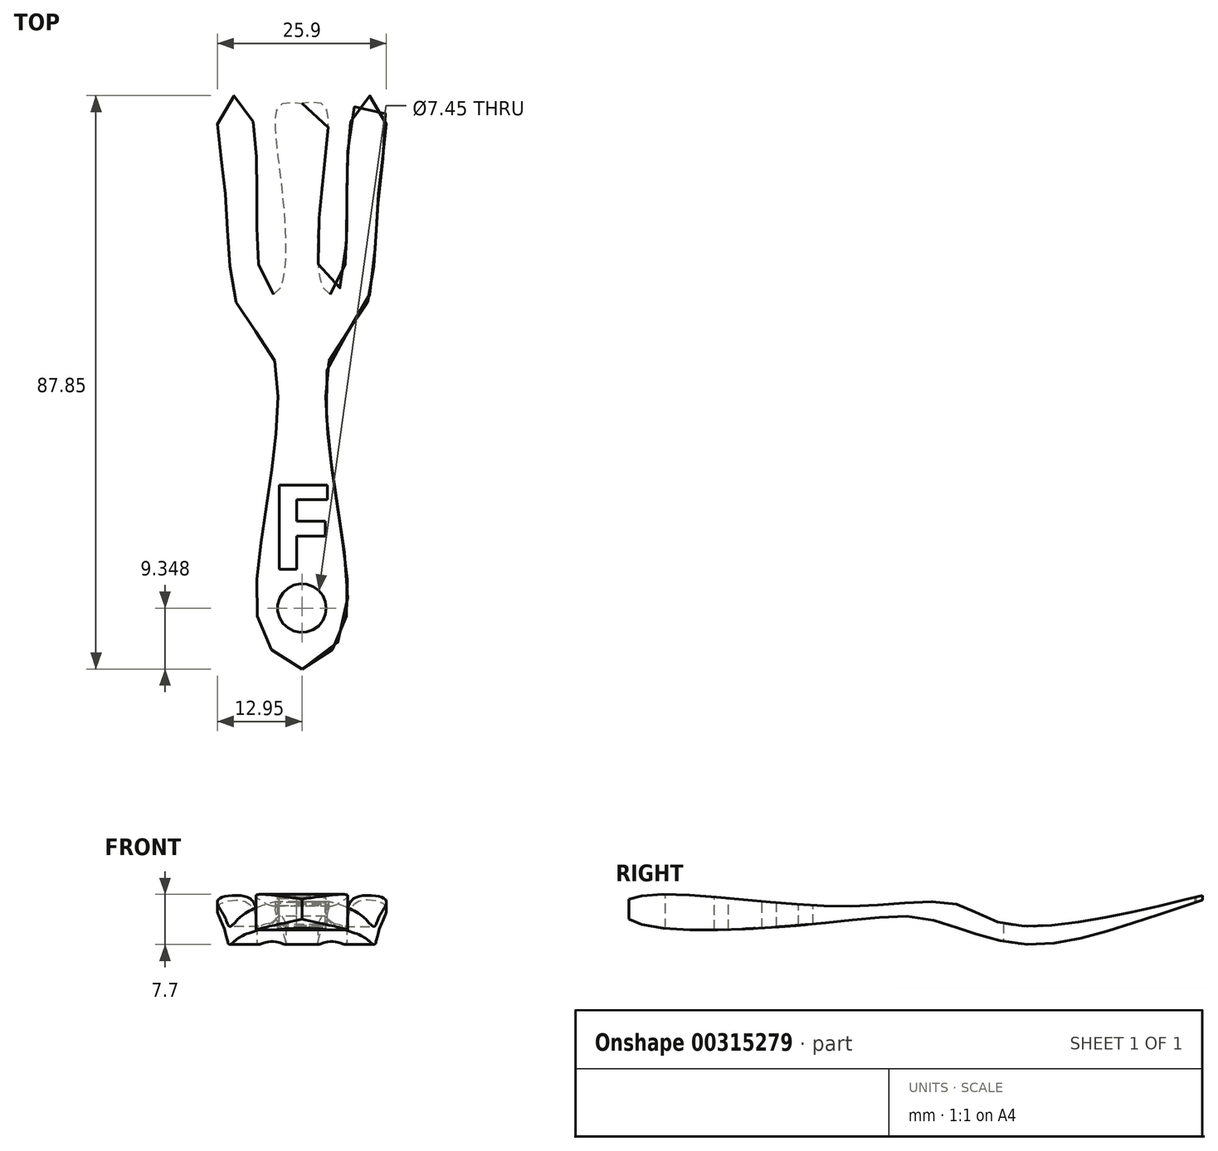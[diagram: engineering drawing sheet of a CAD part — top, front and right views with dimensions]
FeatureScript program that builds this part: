
annotation { "Feature Type Name" : "Feature", "Feature Type Description" : "" }
export const myFeature = defineFeature(function(context is Context, id is Id, definition is map)
    precondition{}
    {
        {
            var Q0;
            Q0=qCreatedBy(makeId("Top.planeOp"),FACE);
            var sketch = newSketch(context, id + "F0", { "sketchPlane" : qUnion([Q0])});
            skLineSegment(sketch, "E0.bottom", {"start": v(15, -50) * mm, "end": v(-15, -50) * mm});
            skLineSegment(sketch, "E0.top", {"start": v(15, 50) * mm, "end": v(-15, 50) * mm});
            skLineSegment(sketch, "E0.left", {"start": v(15, -50) * mm, "end": v(15, 50) * mm});
            skLineSegment(sketch, "E0.right", {"start": v(-15, -50) * mm, "end": v(-15, 50) * mm});
            skPoint(sketch, "E0.middle", {"position": v(0, 0) * mm});
            skSolve(sketch);
        }
        {
            var Q0;
            Q0=makeQuery(id+"F0.imprint","IMPRINT",FACE,{"disambiguationData":[TD([[makeQuery(id+"F0.imprint","IMPRINT",EDGE,{"derivedFrom":sQuery(id+"F0.wireOp",EDGE,"E0.bottom")}),-1.0]])]});
            extrude(context, id + "F1", {"entities" : qUnion([Q0]), "depth" : 30 * mm});
        }
        {
            var Q0;
            Q0=makeQuery(id+"F1.opExtrude","CAP_FACE",FACE,{"disambiguationData":[OSD([sQuery(id+"F0.wireOp",EDGE,"E0.bottom"),sQuery(id+"F0.wireOp",EDGE,"E0.top"),sQuery(id+"F0.wireOp",EDGE,"E0.left"),sQuery(id+"F0.wireOp",EDGE,"E0.right")])],"isStart":false});
            var sketch = newSketch(context, id + "F2", { "sketchPlane" : qUnion([Q0])});
            skFitSpline(sketch, "E1", {"points": [v(0, 40.8) * mm, v(3.4, 40.5) * mm, v(3.12, 28.61) * mm, v(3.68, 11.9) * mm, v(5.95, 12.75) * mm, v(8.5, 41.07) * mm, v(12.18, 40.8) * mm, v(11.9, 28.61) * mm, v(9.35, 8.5) * mm, v(4.58, 2.67) * mm, v(5.67, -22.38) * mm, v(6.52, -39.37) * mm, v(0, -45.9) * mm], "startDerivative": vector(88.79, 5.75) * mm, "endDerivative": vector(-156.65, -61.24) * mm});
            skLineSegment(sketch, "E2", {"start": v(0, 40.8) * mm, "end": v(0, -45.9) * mm, "construction": true});
            skFitSpline(sketch, "E3.MirrorCS", {"points": [v(0, 40.8) * mm, v(-3.4, 40.5) * mm, v(-3.12, 28.61) * mm, v(-3.68, 11.9) * mm, v(-5.95, 12.75) * mm, v(-8.5, 41.07) * mm, v(-12.18, 40.8) * mm, v(-11.9, 28.61) * mm, v(-9.35, 8.5) * mm, v(-4.58, 2.67) * mm, v(-5.67, -22.38) * mm, v(-6.52, -39.37) * mm, v(0, -45.9) * mm], "startDerivative": vector(-88.79, 5.75) * mm, "endDerivative": vector(156.65, -61.24) * mm});
            skSolve(sketch);
        }
        {
            var Q0;
            Q0=makeQuery(id+"F1.opExtrude","SWEPT_FACE",FACE,{"disambiguationData":[OSD([sQuery(id+"F0.wireOp",EDGE,"E0.left")])]});
            var sketch = newSketch(context, id + "F3", { "sketchPlane" : qUnion([Q0])});
            skPoint(sketch, "E4.7.internal.snap0", {"position": v(0, 30) * mm});
            skFitSpline(sketch, "E4", {"points": [v(45.9, 22.1) * mm, v(15.01, 16.43) * mm, v(4.25, 19.83) * mm, v(-14.45, 19.55) * mm, v(-46.17, 20.4) * mm, v(-45.9, 17.56) * mm, v(-12.75, 17.28) * mm, v(0, 17.56) * mm, v(12.75, 13.88) * mm, v(30.6, 16.71) * mm, v(45.9, 22.1) * mm]});
            skSolve(sketch);
        }
        {
            var Q0;
            Q0=makeQuery(id+"F3.imprint","IMPRINT",FACE,{"disambiguationData":[TD([[makeQuery(id+"F3.imprint","IMPRINT",EDGE,{"derivedFrom":sQuery(id+"F3.wireOp",EDGE,"E4")}),-1.0]])]});
            extrude(context, id + "F4", {"entities" : qUnion([Q0]), "operationType" : NewBodyOperationType.REMOVE, "oppositeDirection" : true, "depth" : 30 * mm});
        }
        {
            var Q0;
            Q0=makeQuery(id+"F2.imprint","IMPRINT",FACE,{"disambiguationData":[TD([[makeQuery(id+"F2.imprint","IMPRINT",EDGE,{"derivedFrom":sQuery(id+"F2.wireOp",EDGE,"E1")}),1.0]])]});
            extrude(context, id + "F5", {"entities" : qUnion([Q0]), "operationType" : NewBodyOperationType.REMOVE, "oppositeDirection" : true, "depth" : 30 * mm});
        }
        {
            var Q0;
            Q0=qCreatedBy(makeId("Top.planeOp"),FACE);
            var sketch = newSketch(context, id + "F6", { "sketchPlane" : qUnion([Q0])});
            skCircle(sketch, "E5", {"center": v(0, -36.54) * mm, "radius": 3.73 * mm});
            skText(sketch, "E6", { "text": "F", "fontName": "OpenSans-Bold.ttf"});
            const initialGuessF6  = {"E6": [-0.0051, -0.0306, 1, 0, 0.01303]};
            skSetInitialGuess(sketch, initialGuessF6);
            skSolve(sketch);
        }
        {
            var Q0;
            Q0 = qSketchRegion(id + "F6", true);
            extrude(context, id + "F7", {"entities" : qUnion([Q0]), "operationType" : NewBodyOperationType.REMOVE, "endBound" : BoundingType.SYMMETRIC, "oppositeDirection" : true, "depth" : 70 * mm});
        }
    });
